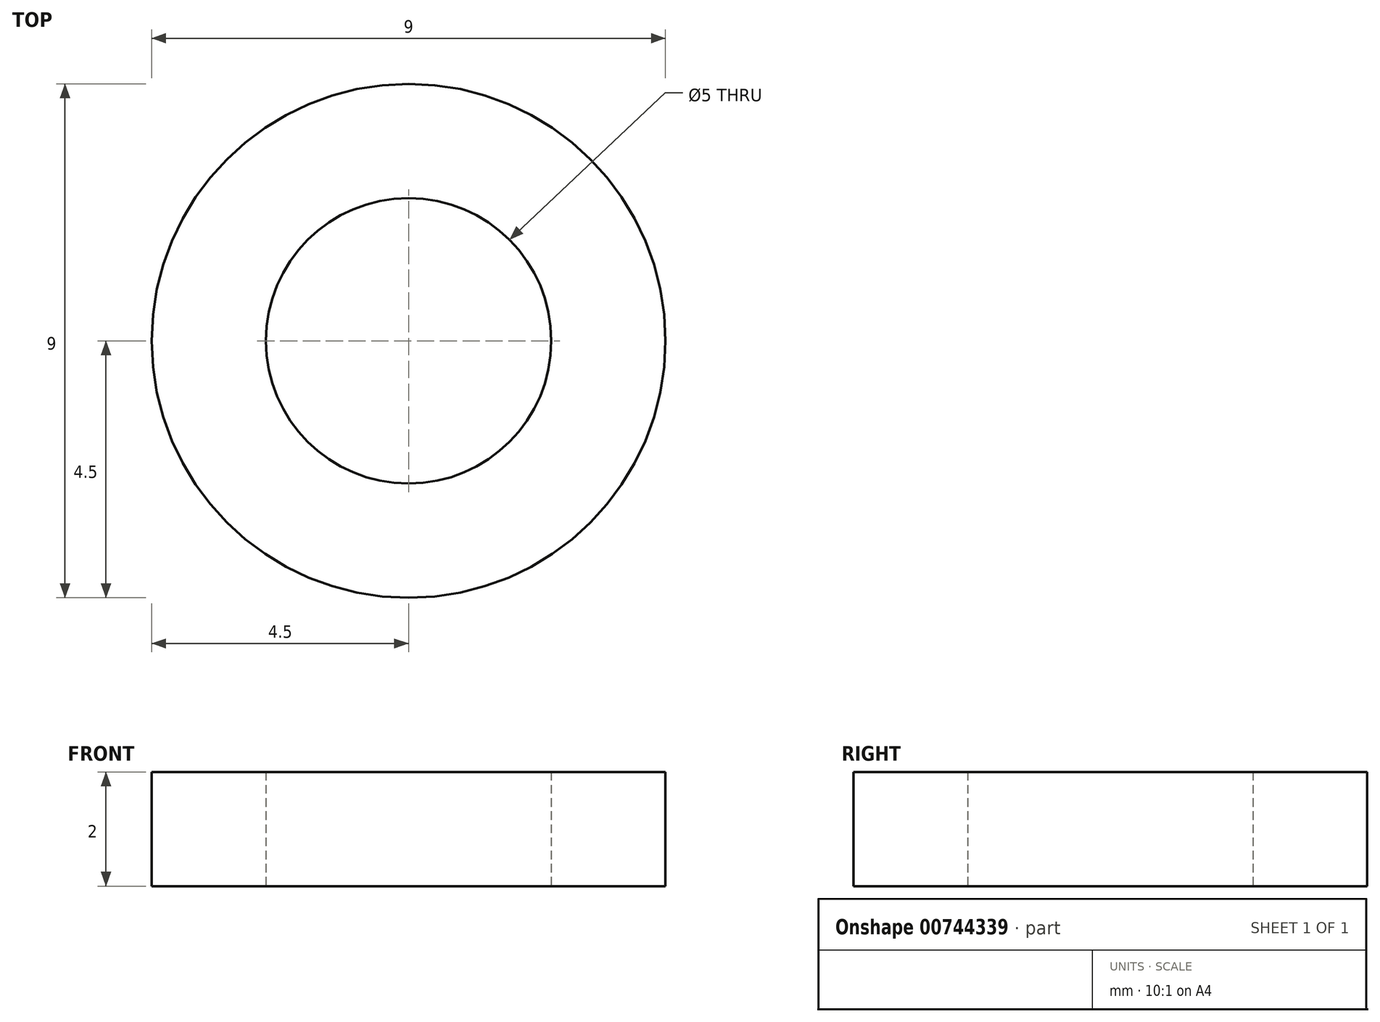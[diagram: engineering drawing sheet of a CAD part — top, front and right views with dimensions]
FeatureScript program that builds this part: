
annotation { "Feature Type Name" : "Feature", "Feature Type Description" : "" }
export const myFeature = defineFeature(function(context is Context, id is Id, definition is map)
    precondition{}
    {
        {
            var Q0;
            Q0=qCreatedBy(makeId("Top.planeOp"),FACE);
            var sketch = newSketch(context, id + "F0", { "sketchPlane" : qUnion([Q0])});
            skCircle(sketch, "E0", {"center": v(0, 0) * mm, "radius": 2.5 * mm});
            skCircle(sketch, "E1", {"center": v(0, 0) * mm, "radius": 4.5 * mm});
            skSolve(sketch);
        }
        {
            var Q0;
            Q0=makeQuery(id+"F0.imprint","IMPRINT",FACE,{"disambiguationData":[TD([[makeQuery(id+"F0.imprint","IMPRINT",EDGE,{"derivedFrom":sQuery(id+"F0.wireOp",EDGE,"E0")}),-1.0]])]});
            extrude(context, id + "F1", {"entities" : qUnion([Q0]), "depth" : 2 * mm, "offsetDistance" : 25 * mm});
        }
    });
